# Revit family: TWINFRESH EXPERT RW1-85-2-V.2
name_source: partatom
category: Оборудование
units: mm (PartAtom-declared; Revit-internal decimal feet)

## family parameters
Всегда вертикально = Да
Классификация = Нет
На основе рабочей плоскости = Нет
Общий = Нет
При загрузке вырезать с полостями = Нет
Размер круглого соединителя = Использовать диаметр
Тип детали = Нормальный
Точка принадлежности помещению = Нет

## types (1)
- RW1-85-2-V.2
    00_20_Виробник = Vents
    00_20_Назва = TwinFresh Expert
    00_20_Тип = RW1-85-2-V.2
    D = 160 мм
    Dy = 156 мм
    L стенна = 150 мм
    l стенна = 75 мм
    Висота = 286 мм
    Довжина = 277 мм
    Діаметр = 160 мм
    Изготовитель = Vents
    Класифікація навантаження = HVAC
    Кількість фаз = 1
    Максимальний потік повітря = 23.6 м³/ч
    Матеріал зони обслуговуваня = <По категории>
    Матеріал корпусу = Пластмасса, непрозрачная, белая
    Напруга = 230 В
    Отметка по умолчанию = 0 мм
    Потужність = 10 Вт
    Рівень звукового тиску на відстані 3 м = 2.1 Sones
    Струм = 0.106 А
    Температура повітря, що переміщається = +5...+104 °С
    Установлена потужність = 24 В·А
    Фільтр = MERV 5, MERV 14 (option)
    Частота = 50 Гц
    Ширина = 310 мм
